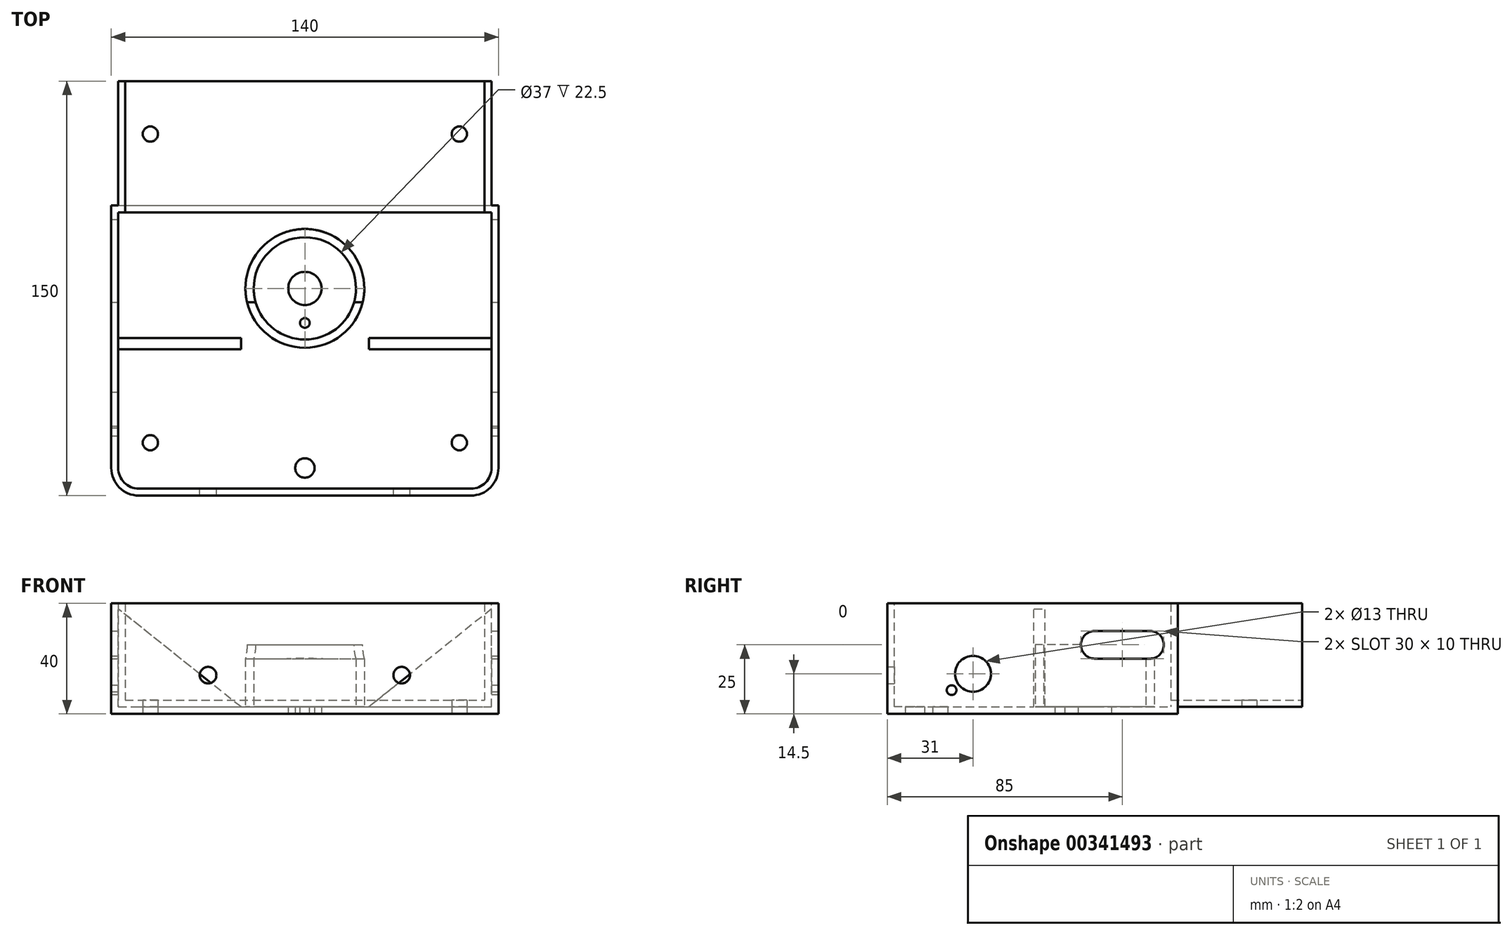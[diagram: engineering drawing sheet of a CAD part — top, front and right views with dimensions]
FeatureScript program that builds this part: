
annotation { "Feature Type Name" : "Feature", "Feature Type Description" : "" }
export const myFeature = defineFeature(function(context is Context, id is Id, definition is map)
    precondition{}
    {
        {
            var Q0;
            Q0=qCreatedBy(makeId("Top.planeOp"),FACE);
            var sketch = newSketch(context, id + "F0", { "sketchPlane" : qUnion([Q0])});
            skLineSegment(sketch, "E0.bottom", {"start": v(-70, -25) * mm, "end": v(70, -25) * mm});
            skLineSegment(sketch, "E0.top", {"start": v(-70, 125) * mm, "end": v(70, 125) * mm});
            skLineSegment(sketch, "E0.left", {"start": v(-70, -25) * mm, "end": v(-70, 125) * mm});
            skLineSegment(sketch, "E0.right", {"start": v(70, -25) * mm, "end": v(70, 125) * mm});
            skSolve(sketch);
        }
        {
            var Q0;
            Q0=makeQuery(id+"F0.imprint","IMPRINT",FACE,{"disambiguationData":[TD([[makeQuery(id+"F0.imprint","IMPRINT",EDGE,{"derivedFrom":sQuery(id+"F0.wireOp",EDGE,"E0.bottom")}),1.0]])]});
            extrude(context, id + "F1", {"entities" : qUnion([Q0]), "depth" : 40 * mm});
        }
        {
            var Q0;
            Q0=makeQuery(id+"F1.opExtrude","SWEPT_EDGE",EDGE,{"disambiguationData":[OSD([sQuery(id+"F0.wireOp",EDGE,"E0.bottom"),sQuery(id+"F0.wireOp",EDGE,"E0.left")])]});
            var Q1;
            Q1=makeQuery(id+"F1.opExtrude","SWEPT_EDGE",EDGE,{"disambiguationData":[OSD([sQuery(id+"F0.wireOp",EDGE,"E0.bottom"),sQuery(id+"F0.wireOp",EDGE,"E0.right")])]});
            fillet(context, id + "F2", {"entities" : qUnion([Q0, Q1]), "radius" : 10 * mm, "tangentPropagation" : true, "allowEdgeOverflow" : false});
        }
        {
            var Q0;
            Q0=qCreatedBy(makeId("Top.planeOp"),FACE);
            var sketch = newSketch(context, id + "F3", { "sketchPlane" : qUnion([Q0])});
            skLineSegment(sketch, "E1.bottom", {"start": v(-100, 180) * mm, "end": v(100, 180) * mm});
            skLineSegment(sketch, "E1.top", {"start": v(-100, 80) * mm, "end": v(100, 80) * mm});
            skLineSegment(sketch, "E1.left", {"start": v(-100, 180) * mm, "end": v(-100, 80) * mm});
            skLineSegment(sketch, "E1.right", {"start": v(100, 180) * mm, "end": v(100, 80) * mm});
            skSolve(sketch);
        }
        {
            var Q0;
            Q0=makeQuery(id+"F3.imprint","IMPRINT",FACE,{"disambiguationData":[TD([[makeQuery(id+"F3.imprint","IMPRINT",EDGE,{"derivedFrom":sQuery(id+"F3.wireOp",EDGE,"E1.bottom")}),-1.0]])]});
            extrude(context, id + "F4", {"entities" : qUnion([Q0]), "operationType" : NewBodyOperationType.REMOVE, "depth" : 2.5 * mm});
        }
        {
            var Q0;
            Q0=qCreatedBy(makeId("Top.planeOp"),FACE);
            var sketch = newSketch(context, id + "F5", { "sketchPlane" : qUnion([Q0])});
            skLineSegment(sketch, "E2.bottom", {"start": v(-107.5, 140) * mm, "end": v(-67.5, 140) * mm});
            skLineSegment(sketch, "E2.top", {"start": v(-107.5, 80) * mm, "end": v(-67.5, 80) * mm});
            skLineSegment(sketch, "E2.left", {"start": v(-107.5, 140) * mm, "end": v(-107.5, 80) * mm});
            skLineSegment(sketch, "E2.right", {"start": v(-67.5, 140) * mm, "end": v(-67.5, 80) * mm});
            skLineSegment(sketch, "E3.bottom", {"start": v(67.5, 140) * mm, "end": v(107.5, 140) * mm});
            skLineSegment(sketch, "E3.top", {"start": v(67.5, 80) * mm, "end": v(107.5, 80) * mm});
            skLineSegment(sketch, "E3.left", {"start": v(67.5, 140) * mm, "end": v(67.5, 80) * mm});
            skLineSegment(sketch, "E3.right", {"start": v(107.5, 140) * mm, "end": v(107.5, 80) * mm});
            skSolve(sketch);
        }
        {
            var Q0;
            Q0=qSketchRegion(id+"F5",true);
            extrude(context, id + "F6", {"entities" : qUnion([Q0]), "operationType" : NewBodyOperationType.REMOVE, "depth" : 200 * mm});
        }
        {
            var Q0;
            Q0=makeQuery(id+"F1.opExtrude","CAP_FACE",FACE,{"disambiguationData":[OSD([sQuery(id+"F0.wireOp",EDGE,"E0.bottom"),sQuery(id+"F0.wireOp",EDGE,"E0.top"),sQuery(id+"F0.wireOp",EDGE,"E0.left"),sQuery(id+"F0.wireOp",EDGE,"E0.right")])],"isStart":false});
            var Q1;
            Q1=makeQuery(id+"F1.opExtrude","SWEPT_FACE",FACE,{"disambiguationData":[OSD([sQuery(id+"F0.wireOp",EDGE,"E0.top")])]});
            shell(context, id + "F7", {"entities" : qUnion([Q0, Q1]), "thickness" : 2.5 * mm});
        }
        {
            var Q0;
            Q0=qCreatedBy(makeId("Top.planeOp"),FACE);
            var sketch = newSketch(context, id + "F8", { "sketchPlane" : qUnion([Q0])});
            skCircle(sketch, "E4", {"center": v(0, 50) * mm, "radius": 6 * mm});
            skSolve(sketch);
        }
        {
            var Q0;
            Q0=makeQuery(id+"F8.imprint","IMPRINT",FACE,{"disambiguationData":[TD([[makeQuery(id+"F8.imprint","IMPRINT",EDGE,{"derivedFrom":sQuery(id+"F8.wireOp",EDGE,"E4")}),1.0]])]});
            extrude(context, id + "F9", {"entities" : qUnion([Q0]), "operationType" : NewBodyOperationType.REMOVE, "depth" : 25 * mm});
        }
        {
            var Q0;
            Q0=qCreatedBy(makeId("Top.planeOp"),FACE);
            var sketch = newSketch(context, id + "F10", { "sketchPlane" : qUnion([Q0])});
            skCircle(sketch, "E5", {"center": v(0, 50) * mm, "radius": 21.5 * mm});
            skCircle(sketch, "E6", {"center": v(0, 50) * mm, "radius": 18.5 * mm});
            skSolve(sketch);
        }
        {
            var Q0;
            Q0=makeQuery(id+"F10.imprint","IMPRINT",FACE,{"disambiguationData":[TD([[makeQuery(id+"F10.imprint","IMPRINT",EDGE,{"derivedFrom":sQuery(id+"F10.wireOp",EDGE,"E5")}),1.0]])]});
            extrude(context, id + "F11", {"entities" : qUnion([Q0]), "operationType" : NewBodyOperationType.ADD, "depth" : 25 * mm});
        }
        {
            var Q0;
            Q0=qCreatedBy(makeId("Top.planeOp"),FACE);
            var sketch = newSketch(context, id + "F12", { "sketchPlane" : qUnion([Q0])});
            skCircle(sketch, "E7", {"center": v(-55.86, -5.86) * mm, "radius": 2.75 * mm});
            skCircle(sketch, "E8", {"center": v(55.86, -5.86) * mm, "radius": 2.75 * mm});
            skLineSegment(sketch, "E9", {"start": v(-55.86, -5.86) * mm, "end": v(0, 50) * mm, "construction": true});
            skLineSegment(sketch, "E10", {"start": v(0, 50) * mm, "end": v(55.86, -5.86) * mm, "construction": true});
            skLineSegment(sketch, "E11", {"start": v(0, 50) * mm, "end": v(55.86, 105.86) * mm, "construction": true});
            skLineSegment(sketch, "E12", {"start": v(0, 50) * mm, "end": v(-55.86, 105.86) * mm});
            skCircle(sketch, "E13", {"center": v(0, 50) * mm, "radius": 79 * mm, "construction": true});
            skCircle(sketch, "E14", {"center": v(55.86, 105.86) * mm, "radius": 2.75 * mm});
            skCircle(sketch, "E15", {"center": v(-55.86, 105.86) * mm, "radius": 2.75 * mm});
            skSolve(sketch);
        }
        {
            var Q0;
            Q0=qSketchRegion(id+"F12",true);
            extrude(context, id + "F13", {"entities" : qUnion([Q0]), "operationType" : NewBodyOperationType.REMOVE, "depth" : 25 * mm});
        }
        {
            var Q0;
            Q0=qCreatedBy(makeId("Right.planeOp"),FACE);
            var sketch = newSketch(context, id + "F14", { "sketchPlane" : qUnion([Q0])});
            skCircle(sketch, "E16", {"center": v(6, 14.5) * mm, "radius": 6.5 * mm});
            skSolve(sketch);
        }
        {
            var Q0;
            Q0=makeQuery(id+"F14.imprint","IMPRINT",FACE,{"disambiguationData":[TD([[makeQuery(id+"F14.imprint","IMPRINT",EDGE,{"derivedFrom":sQuery(id+"F14.wireOp",EDGE,"E16")}),1.0]])]});
            extrude(context, id + "F15", {"entities" : qUnion([Q0]), "operationType" : NewBodyOperationType.REMOVE, "oppositeDirection" : true, "depth" : 300 * mm, "hasSecondDirection" : true, "secondDirectionOppositeDirection" : false, "secondDirectionDepth" : 300 * mm});
        }
        {
            var Q0;
            Q0=qCreatedBy(makeId("Front.planeOp"),FACE);
            var sketch = newSketch(context, id + "F16", { "sketchPlane" : qUnion([Q0])});
            skCircle(sketch, "E17", {"center": v(-35, 14) * mm, "radius": 3 * mm});
            skCircle(sketch, "E18", {"center": v(35, 14) * mm, "radius": 3 * mm});
            skSolve(sketch);
        }
        {
            var Q0;
            Q0=makeQuery(id+"F16.imprint","IMPRINT",FACE,{"disambiguationData":[TD([[makeQuery(id+"F16.imprint","IMPRINT",EDGE,{"derivedFrom":sQuery(id+"F16.wireOp",EDGE,"E17")}),1.0]])]});
            var Q1;
            Q1=makeQuery(id+"F16.imprint","IMPRINT",FACE,{"disambiguationData":[TD([[makeQuery(id+"F16.imprint","IMPRINT",EDGE,{"derivedFrom":sQuery(id+"F16.wireOp",EDGE,"E18")}),1.0]])]});
            extrude(context, id + "F17", {"entities" : qUnion([Q0, Q1]), "operationType" : NewBodyOperationType.REMOVE, "depth" : 200 * mm});
        }
        {
            var Q0;
            Q0=qCreatedBy(makeId("Right.planeOp"),FACE);
            var sketch = newSketch(context, id + "F18", { "sketchPlane" : qUnion([Q0])});
            skCircle(sketch, "E19", {"center": v(6, 22) * mm, "radius": 15.5 * mm, "construction": true});
            skCircle(sketch, "E20", {"center": v(-1.75, 8.58) * mm, "radius": 1.75 * mm});
            skLineSegment(sketch, "E21", {"start": v(6, 22) * mm, "end": v(-1.75, 8.58) * mm, "construction": true});
            skLineSegment(sketch, "E22", {"start": v(6, 22) * mm, "end": v(6, -15.46) * mm, "construction": true});
            skCircle(sketch, "E23", {"center": v(6, 22) * mm, "radius": 1 * mm});
            skSolve(sketch);
        }
        {
            var Q0;
            Q0=makeQuery(id+"F18.imprint","IMPRINT",FACE,{"disambiguationData":[TD([[makeQuery(id+"F18.imprint","IMPRINT",EDGE,{"derivedFrom":sQuery(id+"F18.wireOp",EDGE,"E20")}),1.0]])]});
            extrude(context, id + "F19", {"entities" : qUnion([Q0]), "operationType" : NewBodyOperationType.REMOVE, "endBound" : BoundingType.SYMMETRIC, "depth" : 400 * mm});
        }
        {
            var Q0;
            Q0=qCreatedBy(makeId("Top.planeOp"),FACE);
            var sketch = newSketch(context, id + "F20", { "sketchPlane" : qUnion([Q0])});
            skCircle(sketch, "E24", {"center": v(0, 50) * mm, "radius": 12.5 * mm, "construction": true});
            skCircle(sketch, "E25", {"center": v(0, 37.5) * mm, "radius": 1.75 * mm});
            skSolve(sketch);
        }
        {
            var Q0;
            Q0=qSketchRegion(id+"F20",true);
            extrude(context, id + "F21", {"entities" : qUnion([Q0]), "operationType" : NewBodyOperationType.REMOVE, "endBound" : BoundingType.SYMMETRIC, "oppositeDirection" : true, "depth" : 25 * mm});
        }
        {
            var Q0;
            Q0=qCreatedBy(makeId("Front.planeOp"),FACE);
            var sketch = newSketch(context, id + "F22", { "sketchPlane" : qUnion([Q0])});
            skLineSegment(sketch, "E26", {"start": v(-70, 0) * mm, "end": v(-20, 0) * mm});
            skLineSegment(sketch, "E27", {"start": v(-20, 0) * mm, "end": v(-70, 40) * mm});
            skLineSegment(sketch, "E28", {"start": v(-70, 40) * mm, "end": v(-70, 0) * mm});
            skLineSegment(sketch, "E29", {"start": v(20, 0) * mm, "end": v(70, 0) * mm});
            skLineSegment(sketch, "E30", {"start": v(70, 0) * mm, "end": v(70, 40) * mm});
            skLineSegment(sketch, "E31", {"start": v(70, 40) * mm, "end": v(20, 0) * mm});
            skSolve(sketch);
        }
        {
            var Q0;
            Q0=qSketchRegion(id+"F22",true);
            extrude(context, id + "F23", {"entities" : qUnion([Q0]), "operationType" : NewBodyOperationType.ADD, "oppositeDirection" : true, "depth" : 32 * mm, "hasSecondDirection" : true, "secondDirectionOppositeDirection" : true, "secondDirectionDepth" : 28 * mm});
        }
        {
            var Q0;
            Q0=qCreatedBy(makeId("Right.planeOp"),FACE);
            var sketch = newSketch(context, id + "F24", { "sketchPlane" : qUnion([Q0])});
            skLineSegment(sketch, "E32.bottom", {"start": v(50, 30) * mm, "end": v(70, 30) * mm});
            skLineSegment(sketch, "E32.top", {"start": v(50, 20) * mm, "end": v(70, 20) * mm});
            skLineSegment(sketch, "E32.left", {"start": v(50, 30) * mm, "end": v(50, 20) * mm});
            skLineSegment(sketch, "E32.right", {"start": v(70, 30) * mm, "end": v(70, 20) * mm});
            skCircle(sketch, "E33", {"center": v(50, 25) * mm, "radius": 5 * mm});
            skCircle(sketch, "E34", {"center": v(70, 25) * mm, "radius": 5 * mm});
            skSolve(sketch);
        }
        {
            var Q0;
            {var subQ0=sQuery(id+"F24.wireOp",EDGE,"E32.left");Q0=makeQuery(id+"F24.imprint","IMPRINT",FACE,{"disambiguationData":[TD([[makeQuery(id+"F24.imprint","IMPRINT",EDGE,{"derivedFrom":subQ0}),-1.0]])]});}
            var Q1;
            {var subQ0=sQuery(id+"F24.wireOp",EDGE,"E32.left");Q1=makeQuery(id+"F24.imprint","IMPRINT",FACE,{"disambiguationData":[TD([[makeQuery(id+"F24.imprint","IMPRINT",EDGE,{"derivedFrom":subQ0}),1.0]])]});}
            var Q2;
            {var subQ0=sQuery(id+"F24.wireOp",EDGE,"E32.bottom");Q2=makeQuery(id+"F24.imprint","IMPRINT",FACE,{"disambiguationData":[TD([[makeQuery(id+"F24.imprint","IMPRINT",EDGE,{"derivedFrom":subQ0}),-1.0]])]});}
            var Q3;
            {var subQ0=sQuery(id+"F24.wireOp",EDGE,"E32.right");Q3=makeQuery(id+"F24.imprint","IMPRINT",FACE,{"disambiguationData":[TD([[makeQuery(id+"F24.imprint","IMPRINT",EDGE,{"derivedFrom":subQ0}),-1.0]])]});}
            var Q4;
            {var subQ0=sQuery(id+"F24.wireOp",EDGE,"E32.right");Q4=makeQuery(id+"F24.imprint","IMPRINT",FACE,{"disambiguationData":[TD([[makeQuery(id+"F24.imprint","IMPRINT",EDGE,{"derivedFrom":subQ0}),1.0]])]});}
            extrude(context, id + "F25", {"entities" : qUnion([Q0, Q1, Q2, Q3, Q4]), "operationType" : NewBodyOperationType.REMOVE, "endBound" : BoundingType.SYMMETRIC, "oppositeDirection" : true, "depth" : 300 * mm});
        }
        {
            var Q0;
            Q0=qCreatedBy(makeId("Top.planeOp"),FACE);
            var sketch = newSketch(context, id + "F26", { "sketchPlane" : qUnion([Q0])});
            skCircle(sketch, "E35", {"center": v(0, -15) * mm, "radius": 3.5 * mm});
            skSolve(sketch);
        }
        {
            var Q0;
            Q0=qSketchRegion(id+"F26",true);
            extrude(context, id + "F27", {"entities" : qUnion([Q0]), "operationType" : NewBodyOperationType.REMOVE, "depth" : 25 * mm});
        }
    });
